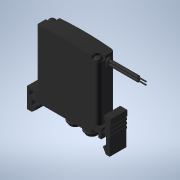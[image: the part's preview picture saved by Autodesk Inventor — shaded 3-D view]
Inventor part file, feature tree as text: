
AUTODESK INVENTOR PART (.ipt)
format: ipt  version: 2024.3 (Build 283343000, 343)  size: 364,544 bytes
history: native  units: mm
features: sketch x18, extrude x10, revolve x8
ambient origin geometry x8: Origin, YZ Plane, XZ Plane, XY Plane, X Axis, Y Axis, Z Axis, Center Point
bodies: Solid1 (feature_tree)
feature tree (36):
  extrude  "Extrusion1"  Depth=9.0mm TaperAngle=0.0deg
  extrude  "Extrusion2"  Depth=3.0mm TaperAngle=0.0deg
  extrude  "Extrusion3"  Depth=1.0mm TaperAngle=0.0deg
  extrude  "Extrusion4"  TaperAngle=360.0deg  [1 undecoded]
  extrude  "Extrusion5"  Depth=0.9mm TaperAngle=0.0deg
  extrude  "Extrusion6"  TaperAngle=360.0deg  [1 undecoded]
  extrude  "Extrusion7"  Depth=2.0mm TaperAngle=0.0deg
  revolve  "Revolution1"  Angle=360.0deg
  revolve  "Revolution2"  Angle=360.0deg
  extrude  "Extrusion8"  [1 undecoded]
  revolve  "Revolution3"  [1 undecoded]
  revolve  "Revolution4"  [1 undecoded]
  extrude  "Extrusion9"  [1 undecoded]
  extrude  "Extrusion10"  [1 undecoded]
  revolve  "Revolution5"  [1 undecoded]
  revolve  "Revolution6"  [1 undecoded]
  revolve  "Revolution7"  [1 undecoded]
  revolve  "Revolution8"  [1 undecoded]
  sketch  "Sketch_7"  dims[d18=360.0deg d19=360.0deg]
  sketch  "Sketch_2"  dims[d0=9.0mm d1=0.0mm d2=31.9mm d3=0.0mm]
  sketch  "Sketch_3"  dims[d4=9.0mm d5=0.0mm d6=3.0mm d7=0.0mm]
  sketch  "Sketch_4"  dims[d8=4.5mm d9=0.0mm d10=1.0mm d11=0.0mm]
  sketch  "Sketch_5"  dims[d12=1.0mm d13=0.0mm d14=360.0deg]
  sketch  "Sketch_6"  dims[d15=360.0deg d16=0.9mm d17=0.0mm]
  sketch  "Sketch_8"  dims[d20=2.0mm d21=0.0mm d22=2.0mm d23=0.0mm]
  sketch  "Sketch_9"  dims[d24=360.0deg d25=360.0deg]
  sketch  "Sketch_10"  dims[d26=360.0deg d27=360.0deg]
  sketch  "Sketch_19"
  sketch  "Sketch_20"
  sketch  "Sketch_21"
  sketch  "Sketch_22"
  sketch  "Sketch_23"
  sketch  "Sketch_24"
  sketch  "Sketch_25"
  sketch  "Sketch_26"
  sketch  "Sketch_27"
note: 11 required parameter values undecoded (feature->parameter linkage not recoverable at this tier; creation-order binding heuristic only, values carry confidence <= 0.55)
